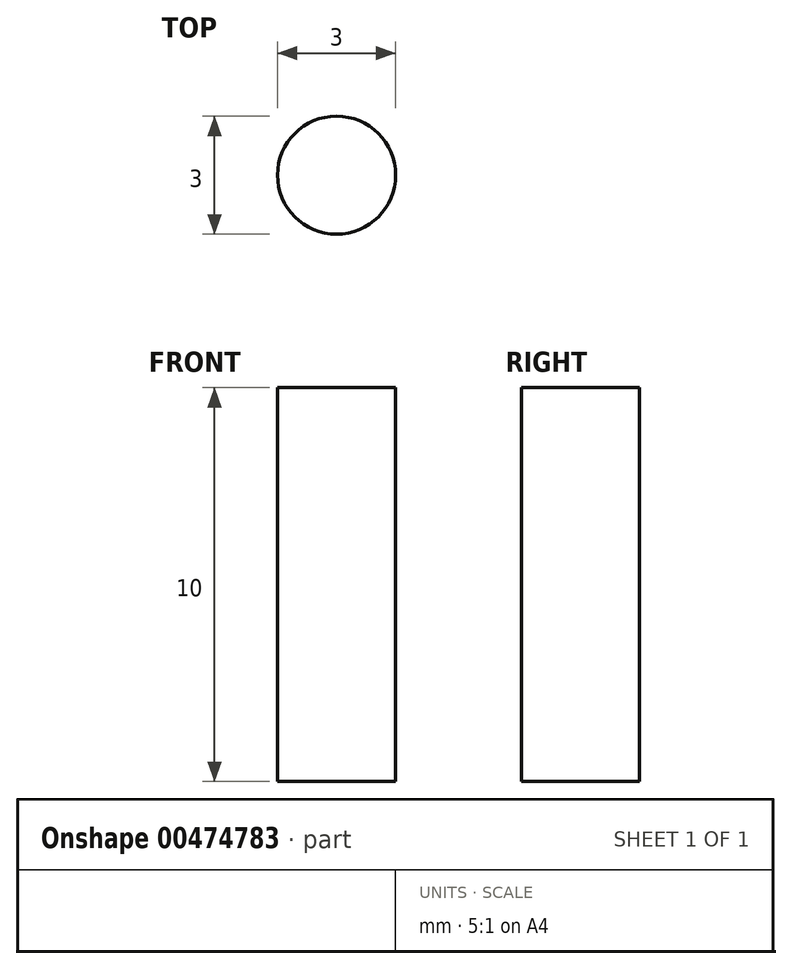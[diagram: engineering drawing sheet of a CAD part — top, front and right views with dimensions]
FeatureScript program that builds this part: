
annotation { "Feature Type Name" : "Feature", "Feature Type Description" : "" }
export const myFeature = defineFeature(function(context is Context, id is Id, definition is map)
    precondition{}
    {
        {
            var Q0;
            Q0=qCreatedBy(makeId("Top.planeOp"),FACE);
            var sketch = newSketch(context, id + "F0", { "sketchPlane" : qUnion([Q0])});
            skCircle(sketch, "E0", {"center": v(0, 0) * mm, "radius": 1.5 * mm});
            skSolve(sketch);
        }
        {
            var Q0;
            Q0=qSketchRegion(id+"F0",true);
            extrude(context, id + "F1", {"entities" : qUnion([Q0]), "depth" : 10 * mm, "offsetDistance" : 25 * mm});
        }
    });
